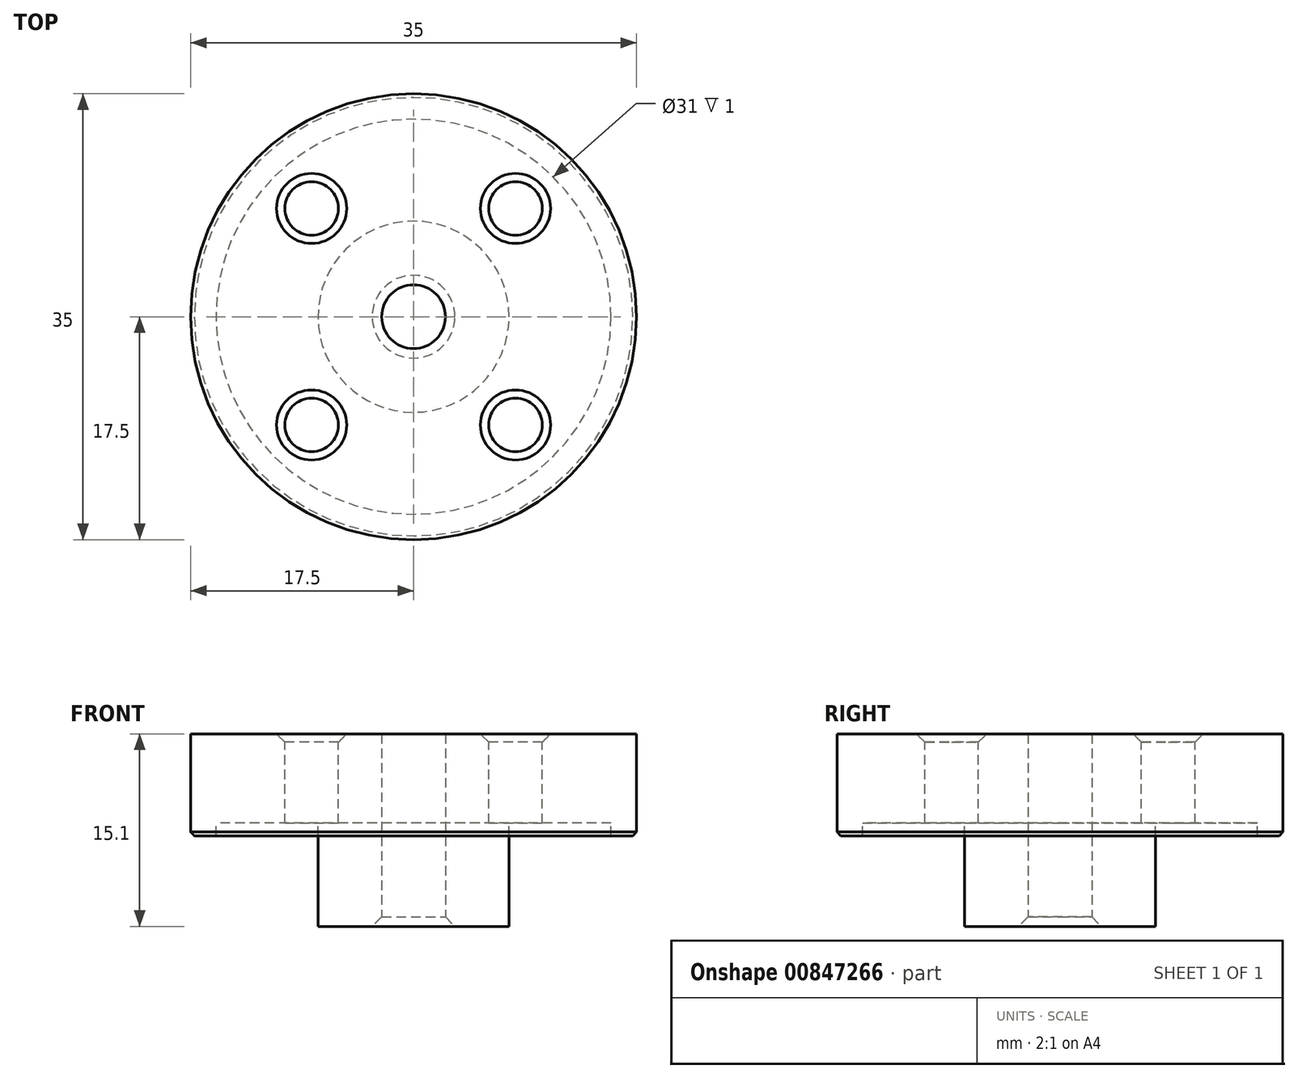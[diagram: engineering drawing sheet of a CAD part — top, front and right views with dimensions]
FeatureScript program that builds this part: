
annotation { "Feature Type Name" : "Feature", "Feature Type Description" : "" }
export const myFeature = defineFeature(function(context is Context, id is Id, definition is map)
    precondition{}
    {
        {
            var Q0;
            Q0=qCreatedBy(makeId("Front.planeOp"),FACE);
            var sketch = newSketch(context, id + "F0", { "sketchPlane" : qUnion([Q0])});
            skLineSegment(sketch, "E0", {"start": v(0, 29.48) * mm, "end": v(0, 14.38) * mm});
            skLineSegment(sketch, "E1", {"start": v(0, 29.48) * mm, "end": v(17.5, 29.48) * mm});
            skLineSegment(sketch, "E2", {"start": v(17.5, 29.48) * mm, "end": v(17.5, 21.48) * mm});
            skLineSegment(sketch, "E3", {"start": v(7.5, 14.38) * mm, "end": v(0, 14.38) * mm});
            skPoint(sketch, "E4.orphan", {"position": v(0, 49.43) * mm});
            skLineSegment(sketch, "E5", {"start": v(17.5, 21.48) * mm, "end": v(15.5, 21.48) * mm});
            skLineSegment(sketch, "E6", {"start": v(15.5, 22.48) * mm, "end": v(15.5, 21.48) * mm});
            skLineSegment(sketch, "E7", {"start": v(15.5, 22.48) * mm, "end": v(7.5, 22.48) * mm});
            skLineSegment(sketch, "E8", {"start": v(7.5, 14.38) * mm, "end": v(7.5, 22.48) * mm});
            skSolve(sketch);
        }
        {
            var Q0;
            Q0=makeQuery(id+"F0.imprint","IMPRINT",FACE,{"disambiguationData":[TD([[makeQuery(id+"F0.imprint","IMPRINT",EDGE,{"derivedFrom":sQuery(id+"F0.wireOp",EDGE,"E0")}),1.0]])]});
            var Q1;
            Q1=sQuery(id+"F0.wireOp",EDGE,"E1");
            var Q2;
            Q2=sQuery(id+"F0.wireOp",EDGE,"E2");
            var Q3;
            Q3=sQuery(id+"F0.wireOp",EDGE,"YHcA4Im3-FS8l-6eyh-U9BE-gC3bYL5cbM2Y");
            var Q4;
            Q4=sQuery(id+"F0.wireOp",EDGE,"8rSnnVvJ-0WPB-2tvv-kjZA-h0GsFayG6xX2");
            var Q5;
            Q5=sQuery(id+"F0.wireOp",EDGE,"ymaaTPRN-pn7h-KTkw-Tj4r-ce4dMD7t58Fd");
            var Q6;
            Q6=sQuery(id+"F0.wireOp",EDGE,"Zvi59vuS-P0h0-SPNf-XehY-vy1T080MsQQi");
            var Q7;
            Q7=sQuery(id+"F0.wireOp",EDGE,"E3");
            var Q8;
            Q8=sQuery(id+"F0.wireOp",EDGE,"E0");
            revolve(context, id + "F1", {"surfaceOperationType" : NewSurfaceOperationType.NEW, "entities" : qUnion([Q0]), "surfaceEntities" : qUnion([Q1, Q2, Q3, Q4, Q5, Q6, Q7]), "axis" : qUnion([Q8]), "revolveType" : RevolveType.FULL});
        }
        {
            var Q0;
            Q0=makeQuery(id+"F1.opRevolve","SWEPT_FACE",FACE,{"disambiguationData":[OSD([sQuery(id+"F0.wireOp",EDGE,"E1")])]});
            var sketch = newSketch(context, id + "F2", { "sketchPlane" : qUnion([Q0])});
            skLineSegment(sketch, "E9", {"start": v(-17.5, 0) * mm, "end": v(17.5, 0) * mm, "construction": true});
            skLineSegment(sketch, "E10", {"start": v(0, 17.5) * mm, "end": v(0, -17.5) * mm, "construction": true});
            skLineSegment(sketch, "E11.0", {"start": v(-8, 17.5) * mm, "end": v(-8, -17.5) * mm, "construction": true});
            skLineSegment(sketch, "E12.0", {"start": v(8, 17.5) * mm, "end": v(8, -17.5) * mm, "construction": true});
            skCircle(sketch, "E13.0", {"center": v(0, 0) * mm, "radius": 22.5 * mm});
            skLineSegment(sketch, "E14.0", {"start": v(-17.5, -8.5) * mm, "end": v(17.5, -8.5) * mm, "construction": true});
            skLineSegment(sketch, "E15.0", {"start": v(-17.5, 8.5) * mm, "end": v(17.5, 8.5) * mm, "construction": true});
            skPoint(sketch, "E16", {"position": v(-8, 8.5) * mm});
            skPoint(sketch, "E17", {"position": v(8, 8.5) * mm});
            skPoint(sketch, "E18", {"position": v(8, -8.5) * mm});
            skPoint(sketch, "E19", {"position": v(-8, -8.5) * mm});
            skSolve(sketch);
        }
        {
            var Q0;
            Q0=sQuery(id+"F2.wireOp",VERTEX,"E16");
            var Q1;
            Q1=sQuery(id+"F2.wireOp",VERTEX,"E17");
            var Q2;
            Q2=sQuery(id+"F2.wireOp",VERTEX,"E18");
            var Q3;
            Q3=sQuery(id+"F2.wireOp",VERTEX,"E19");
            var Q4;
            Q4=makeQuery(id+"F1.opRevolve","SWEPT_BODY",BODY,{"disambiguationData":[OSD([sQuery(id+"F0.wireOp",EDGE,"E0"),sQuery(id+"F0.wireOp",EDGE,"E1"),sQuery(id+"F0.wireOp",EDGE,"E2"),sQuery(id+"F0.wireOp",EDGE,"E3"),sQuery(id+"F0.wireOp",EDGE,"E5"),sQuery(id+"F0.wireOp",EDGE,"E6"),sQuery(id+"F0.wireOp",EDGE,"E7"),sQuery(id+"F0.wireOp",EDGE,"E8")])]});
            hole(context, id + "F3", {"style" : HoleStyle.C_SINK, "endStyle" : HoleEndStyle.THROUGH, "holeDiameter" : 4.2 * mm, "cSinkDiameter" : 5.5 * mm, "cSinkAngle" : 90 * degree, "majorDiameter" : 3 * mm, "isTappedThrough" : true, "tappedDepth" : 12 * mm, "tapClearance" : 3, "locations" : qUnion([Q0, Q1, Q2, Q3]), "scope" : qUnion([Q4])});
        }
        {
            var Q0;
            Q0=makeQuery(id+"F1.opRevolve","SWEPT_FACE",FACE,{"disambiguationData":[OSD([sQuery(id+"F0.wireOp",EDGE,"E3")])]});
            var sketch = newSketch(context, id + "F4", { "sketchPlane" : qUnion([Q0])});
            skPoint(sketch, "E20", {"position": v(0, 0) * mm});
            skSolve(sketch);
        }
        {
            var Q0;
            Q0=sQuery(id+"F4.wireOp",VERTEX,"E20");
            var Q1;
            Q1=makeQuery(id+"F1.opRevolve","SWEPT_BODY",BODY,{"disambiguationData":[OSD([sQuery(id+"F0.wireOp",EDGE,"E0"),sQuery(id+"F0.wireOp",EDGE,"E1"),sQuery(id+"F0.wireOp",EDGE,"E2"),sQuery(id+"F0.wireOp",EDGE,"E3"),sQuery(id+"F0.wireOp",EDGE,"E5"),sQuery(id+"F0.wireOp",EDGE,"E6"),sQuery(id+"F0.wireOp",EDGE,"E7"),sQuery(id+"F0.wireOp",EDGE,"E8")])]});
            hole(context, id + "F5", {"style" : HoleStyle.C_SINK, "endStyle" : HoleEndStyle.THROUGH, "holeDiameter" : 5 * mm, "cSinkDiameter" : 6.5 * mm, "cSinkAngle" : 90 * degree, "majorDiameter" : 6 * mm, "isTappedThrough" : true, "tappedDepth" : 12 * mm, "tapClearance" : 3, "locations" : qUnion([Q0]), "scope" : qUnion([Q1])});
        }
        {
            var Q0;
            Q0=makeQuery(id+"F1.opRevolve","SWEPT_EDGE",EDGE,{"disambiguationData":[OSD([sQuery(id+"F0.wireOp",EDGE,"E2"),sQuery(id+"F0.wireOp",EDGE,"E5")])]});
            chamfer(context, id + "F6", {"entities" : qUnion([Q0]), "width" : 0.3 * mm, "tangentPropagation" : true});
        }
    });
